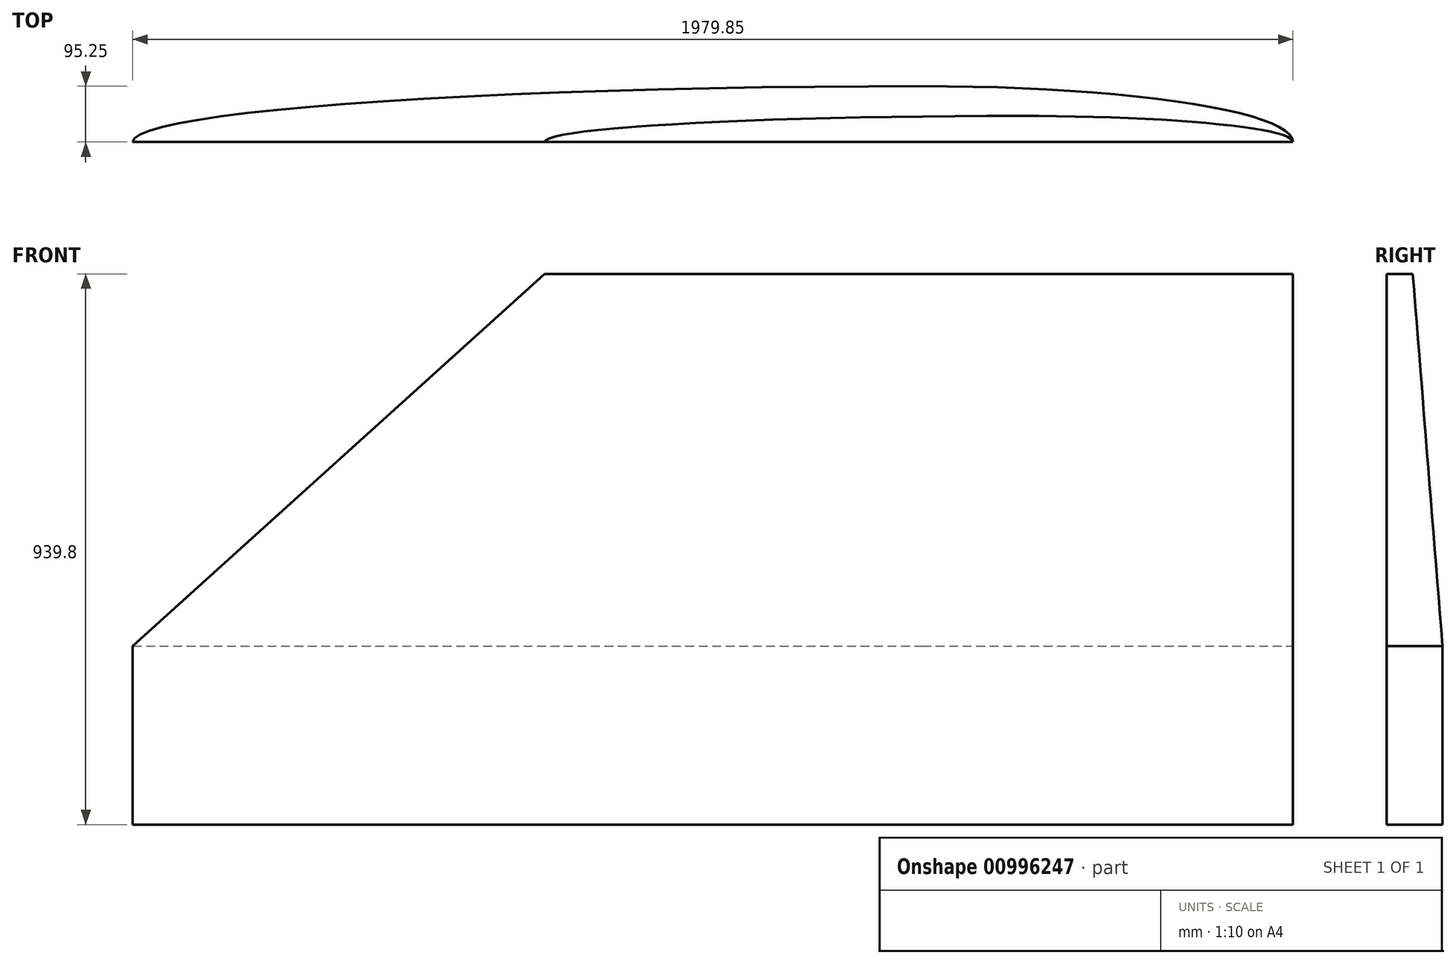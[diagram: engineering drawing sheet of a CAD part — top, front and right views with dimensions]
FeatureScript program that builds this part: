
annotation { "Feature Type Name" : "Feature", "Feature Type Description" : "" }
export const myFeature = defineFeature(function(context is Context, id is Id, definition is map)
    precondition{}
    {
        {
            var Q0;
            Q0=qCreatedBy(makeId("Top.planeOp"),FACE);
            var sketch = newSketch(context, id + "F0", { "sketchPlane" : qUnion([Q0])});
            skLineSegment(sketch, "E0", {"start": v(-918.14, 0) * mm, "end": v(1061.71, 0) * mm});
            skEllipticalArc(sketch, "E1", {});
            skEllipticalArc(sketch, "E2", {});
            const initialGuessF0  = {"E1": [0.42925884356946553, 0, 1, 0, 0.6324533282408253, 0.09525, 0, 1.5707963267948966], "E2": [0.42925884356946553, 0, -1, 0, 1.347400471759175, 0.09525, 4.71238898038469, 0]};
            skSetInitialGuess(sketch, initialGuessF0);
            skSolve(sketch);
        }
        {
            var Q0;
            Q0 = qSketchRegion(id + "F0", true);
            extrude(context, id + "F1", {"entities" : qUnion([Q0]), "depth" : 304.8 * mm, "offsetDistance" : 25.4 * mm});
        }
        {
            var Q0;
            Q0=makeQuery(id+"F1.opExtrude","CAP_FACE",FACE,{"disambiguationData":[OSD([sQuery(id+"F0.wireOp",EDGE,"E0"),sQuery(id+"F0.wireOp",EDGE,"E1"),sQuery(id+"F0.wireOp",EDGE,"E2")])],"isStart":false});
            var sketch = newSketch(context, id + "F2", { "sketchPlane" : qUnion([Q0])});
            skLineSegment(sketch, "E3", {"start": v(1061.71, 0) * mm, "end": v(-215.12, 0) * mm});
            skLineSegment(sketch, "E4", {"start": v(595.18, 0) * mm, "end": v(595.18, 44.45) * mm});
            skEllipticalArc(sketch, "E5", {});
            skEllipticalArc(sketch, "E6", {});
            const initialGuessF2  = {"E5": [0.595179557800293, 0, 1, 0, 0.4665326140099979, 0.04445, 0, 1.5707963267948966], "E6": [0.595179557800293, 0, -1, 0, 0.8102999859900022, 0.04445, 4.71238898038469, 0]};
            skSetInitialGuess(sketch, initialGuessF2);
            skSolve(sketch);
        }
        {
            var Q0;
            {var subQ2=sQuery(id+"F2.wireOp",EDGE,"E4");Q0=makeQuery(id+"F2.imprint","IMPRINT",FACE,{"disambiguationData":[TD([[makeQuery(id+"F2.imprint","IMPRINT",EDGE,{"derivedFrom":subQ2}),1.0]])]});}
            var Q1;
            {var subQ2=sQuery(id+"F2.wireOp",EDGE,"E4");Q1=makeQuery(id+"F2.imprint","IMPRINT",FACE,{"disambiguationData":[TD([[makeQuery(id+"F2.imprint","IMPRINT",EDGE,{"derivedFrom":subQ2}),-1.0]])]});}
            extrude(context, id + "F3", {"entities" : qUnion([Q0, Q1]), "operationType" : NewBodyOperationType.ADD, "depth" : 635 * mm, "offsetDistance" : 25.4 * mm});
        }
        {
            var Q1;
            Q1=makeQuery(id+"F1.opExtrude","CAP_FACE",FACE,{"disambiguationData":[OSD([sQuery(id+"F0.wireOp",EDGE,"E0"),sQuery(id+"F0.wireOp",EDGE,"E1"),sQuery(id+"F0.wireOp",EDGE,"E2")])],"isStart":false});
            var Q2;
            Q2=makeQuery(id+"F3.opExtrude","CAP_FACE",FACE,{"disambiguationData":[OSD([sQuery(id+"F2.wireOp",EDGE,"E3"),sQuery(id+"F2.wireOp",EDGE,"E5"),sQuery(id+"F2.wireOp",EDGE,"E6")])],"isStart":false});
            loft(context, id + "F4", {"operationType" : NewBodyOperationType.ADD, "sheetProfilesArray" : [{ "sheetProfileEntities" : qUnion([Q1]) }, { "sheetProfileEntities" : qUnion([Q2]) }]});
        }
    });
